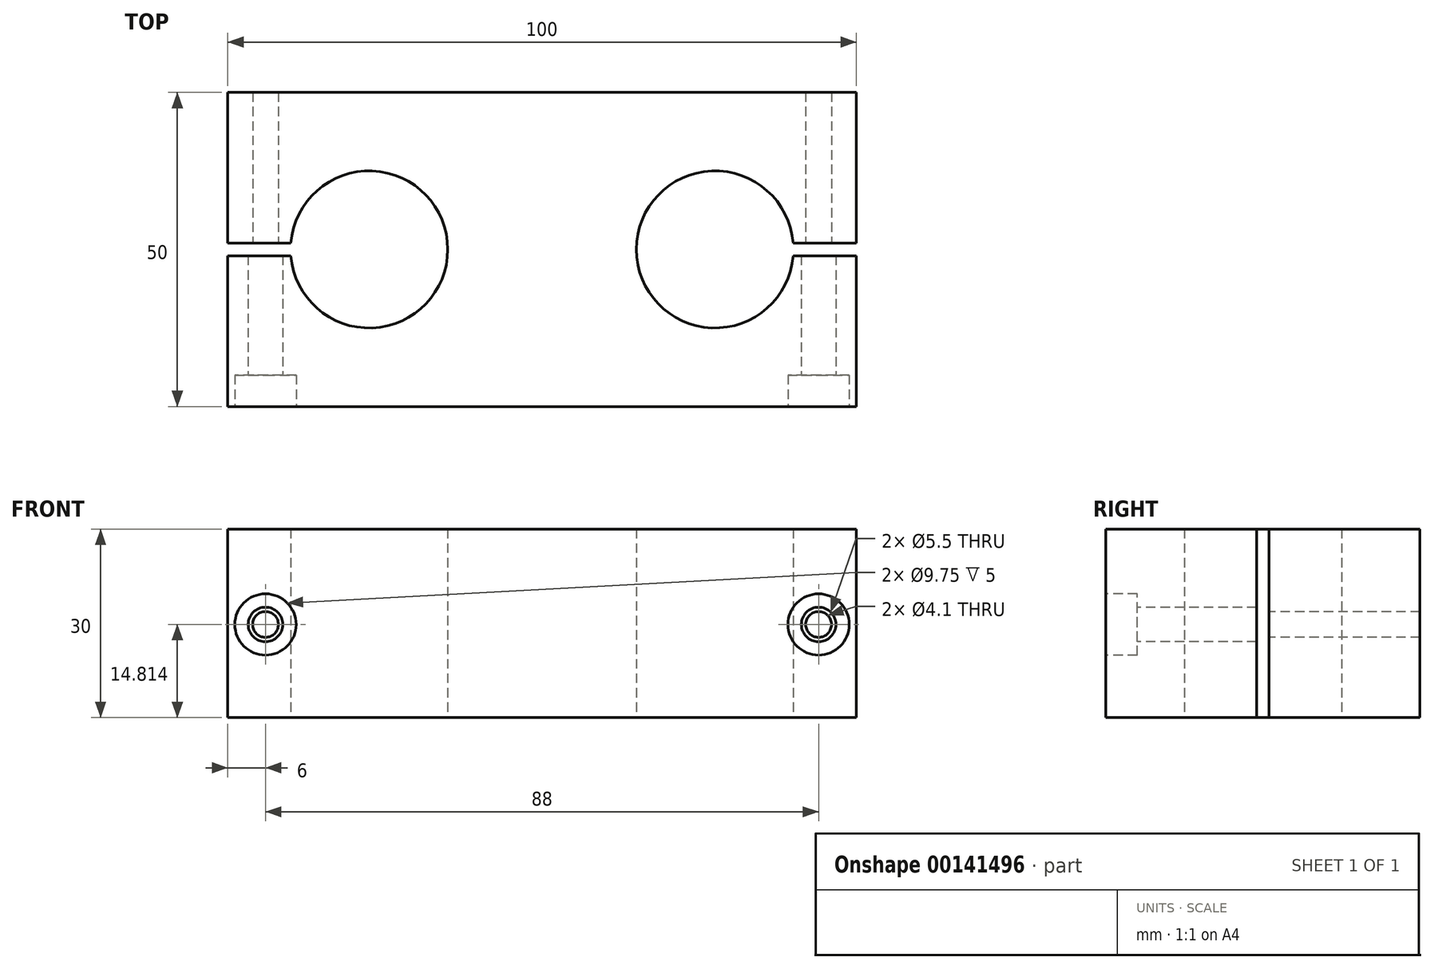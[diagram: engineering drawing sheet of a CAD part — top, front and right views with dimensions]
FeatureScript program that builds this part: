
annotation { "Feature Type Name" : "Feature", "Feature Type Description" : "" }
export const myFeature = defineFeature(function(context is Context, id is Id, definition is map)
    precondition{}
    {
        {
            var Q0;
            Q0=qCreatedBy(makeId("Top.planeOp"),FACE);
            var sketch = newSketch(context, id + "F0", { "sketchPlane" : qUnion([Q0])});
            skLineSegment(sketch, "E0.bottom", {"start": v(50, 25) * mm, "end": v(-50, 25) * mm});
            skLineSegment(sketch, "E0.top", {"start": v(50, -25) * mm, "end": v(-50, -25) * mm});
            skLineSegment(sketch, "E0.left", {"start": v(50, 25) * mm, "end": v(50, 1) * mm});
            skLineSegment(sketch, "E0.right", {"start": v(-50, 25) * mm, "end": v(-50, 1) * mm});
            skPoint(sketch, "E0.middle", {"position": v(0, 0) * mm});
            skArc(sketch, "E1", {"start": v(-39.96, -1) * mm, "mid": v(-15, 0) * mm, "end": v(-39.96, 1) * mm});
            skArc(sketch, "E2", {"start": v(39.96, 1) * mm, "mid": v(15, 0) * mm, "end": v(39.96, -1) * mm});
            skLineSegment(sketch, "E3", {"start": v(-50, 1) * mm, "end": v(-39.96, 1) * mm});
            skLineSegment(sketch, "E4", {"start": v(-50, -1) * mm, "end": v(-39.96, -1) * mm});
            skLineSegment(sketch, "E5", {"start": v(39.96, 1) * mm, "end": v(50, 1) * mm});
            skLineSegment(sketch, "E6", {"start": v(39.96, -1) * mm, "end": v(50, -1) * mm});
            skLineSegment(sketch, "E7.trimOffspring", {"start": v(-50, -1) * mm, "end": v(-50, -25) * mm});
            skLineSegment(sketch, "E8.trimOffspring", {"start": v(50, -1) * mm, "end": v(50, -25) * mm});
            skSolve(sketch);
        }
        {
            var Q0;
            Q0 = qSketchRegion(id + "F0", true);
            extrude(context, id + "F1", {"entities" : qUnion([Q0]), "depth" : 30 * mm});
        }
        {
            var Q0;
            Q0=makeQuery(id+"F1.opExtrude","SWEPT_FACE",FACE,{"disambiguationData":[OSD([sQuery(id+"F0.wireOp",EDGE,"E0.top")])]});
            var sketch = newSketch(context, id + "F2", { "sketchPlane" : qUnion([Q0])});
            skPoint(sketch, "E9", {"position": v(-44, 14.81) * mm});
            skPoint(sketch, "E10", {"position": v(44, 14.81) * mm});
            skSolve(sketch);
        }
        {
            var Q0;
            Q0=sQuery(id+"F2.wireOp",VERTEX,"E9");
            var Q1;
            Q1=sQuery(id+"F2.wireOp",VERTEX,"E10");
            var Q2;
            Q2=makeQuery(id+"F1.opExtrude","SWEPT_BODY",BODY,{"disambiguationData":[OSD([sQuery(id+"F0.wireOp",EDGE,"E0.bottom"),sQuery(id+"F0.wireOp",EDGE,"E0.top"),sQuery(id+"F0.wireOp",EDGE,"E0.left"),sQuery(id+"F0.wireOp",EDGE,"E0.right"),sQuery(id+"F0.wireOp",EDGE,"E1"),sQuery(id+"F0.wireOp",EDGE,"E2"),sQuery(id+"F0.wireOp",EDGE,"E3"),sQuery(id+"F0.wireOp",EDGE,"E4"),sQuery(id+"F0.wireOp",EDGE,"E5"),sQuery(id+"F0.wireOp",EDGE,"E6"),sQuery(id+"F0.wireOp",EDGE,"E7.trimOffspring"),sQuery(id+"F0.wireOp",EDGE,"E8.trimOffspring")])]});
            hole(context, id + "F3", {"style" : HoleStyle.C_BORE, "endStyle" : HoleEndStyle.BLIND, "standardTappedOrClearance" : lookupTablePath({ "standard" : "ISO", "fit" : "Normal", "size" : "M5", "type" : "Clearance" }), "standardBlindInLast" : lookupTablePath({ "fit" : "Standard", "standard" : "ISO", "size" : "M5", "type" : "Clearance" }), "holeDiameter" : 5.5 * mm, "cBoreDiameter" : 9.75 * mm, "cBoreDepth" : 5 * mm, "holeDepth" : 25 * mm, "locations" : qUnion([Q0, Q1]), "scope" : qUnion([Q2])});
        }
        {
            var Q0;
            Q0=makeQuery(id+"F1.opExtrude","SWEPT_FACE",FACE,{"disambiguationData":[OSD([sQuery(id+"F0.wireOp",EDGE,"E3")])]});
            var sketch = newSketch(context, id + "F4", { "sketchPlane" : qUnion([Q0])});
            skPoint(sketch, "E11", {"position": v(-44, 14.81) * mm});
            skPoint(sketch, "E12", {"position": v(44, 14.81) * mm});
            skSolve(sketch);
        }
        {
            var Q0;
            Q0=sQuery(id+"F4.wireOp",VERTEX,"E11");
            var Q1;
            Q1=sQuery(id+"F4.wireOp",VERTEX,"E12");
            var Q2;
            Q2=makeQuery(id+"F1.opExtrude","SWEPT_BODY",BODY,{"disambiguationData":[OSD([sQuery(id+"F0.wireOp",EDGE,"E0.bottom"),sQuery(id+"F0.wireOp",EDGE,"E0.top"),sQuery(id+"F0.wireOp",EDGE,"E0.left"),sQuery(id+"F0.wireOp",EDGE,"E0.right"),sQuery(id+"F0.wireOp",EDGE,"E1"),sQuery(id+"F0.wireOp",EDGE,"E2"),sQuery(id+"F0.wireOp",EDGE,"E3"),sQuery(id+"F0.wireOp",EDGE,"E4"),sQuery(id+"F0.wireOp",EDGE,"E5"),sQuery(id+"F0.wireOp",EDGE,"E6"),sQuery(id+"F0.wireOp",EDGE,"E7.trimOffspring"),sQuery(id+"F0.wireOp",EDGE,"E8.trimOffspring")])]});
            hole(context, id + "F5", {"style" : HoleStyle.SIMPLE, "endStyle" : HoleEndStyle.THROUGH, "standardTappedOrClearance" : lookupTablePath({ "standard" : "ISO", "engagement" : "75%", "pitch" : "0.9 mm", "size" : "M5", "type" : "Tapped" }), "standardBlindInLast" : lookupTablePath({ "standard" : "ISO", "engagement" : "75%", "pitch" : "0.9 mm", "size" : "M5", "type" : "Tapped" }), "holeDiameter" : 4.1 * mm, "startFromSketch" : true, "locations" : qUnion([Q0, Q1]), "scope" : qUnion([Q2]), "isTappedThrough" : true, "showTappedDepth" : true});
        }
    });
